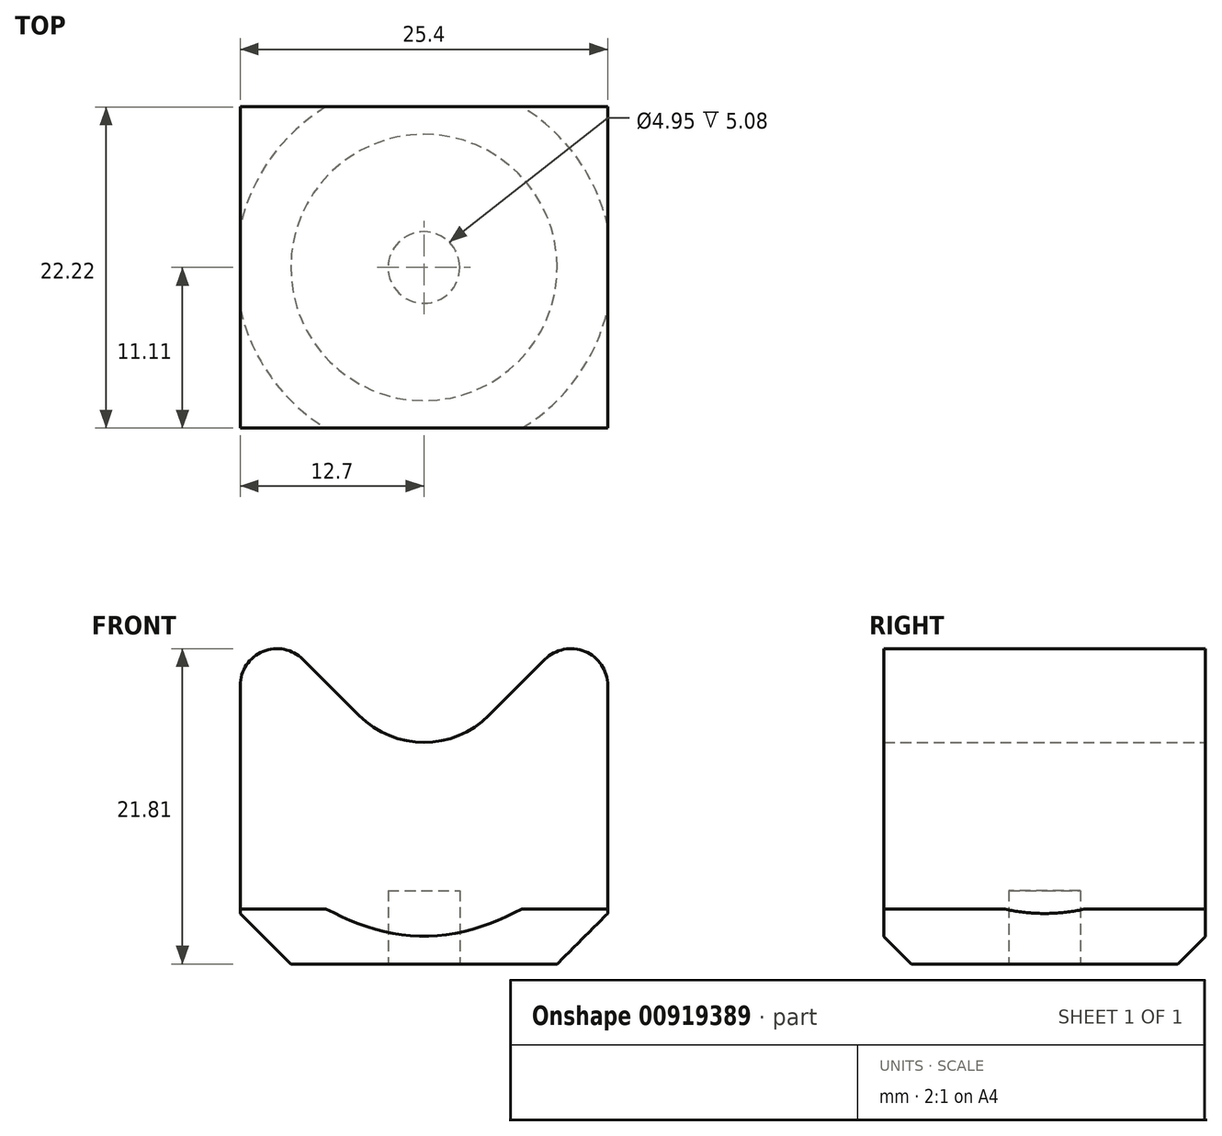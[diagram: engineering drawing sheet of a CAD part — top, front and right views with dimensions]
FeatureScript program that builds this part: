
annotation { "Feature Type Name" : "Feature", "Feature Type Description" : "" }
export const myFeature = defineFeature(function(context is Context, id is Id, definition is map)
    precondition{}
    {
        {
            var Q0;
            Q0=qCreatedBy(makeId("Front.planeOp"),FACE);
            var sketch = newSketch(context, id + "F0", { "sketchPlane" : qUnion([Q0])});
            skLineSegment(sketch, "E0", {"start": v(0, 59) * mm, "end": v(0, -63.05) * mm, "construction": true});
            skLineSegment(sketch, "E1.bottom", {"start": v(-12.7, 12.7) * mm, "end": v(12.7, 12.7) * mm});
            skLineSegment(sketch, "E1.top", {"start": v(-12.7, -12.7) * mm, "end": v(12.7, -12.7) * mm});
            skLineSegment(sketch, "E1.left", {"start": v(-12.7, 12.7) * mm, "end": v(-12.7, -12.7) * mm});
            skLineSegment(sketch, "E1.right", {"start": v(12.7, 12.7) * mm, "end": v(12.7, -12.7) * mm});
            skPoint(sketch, "E1.middle", {"position": v(0, 0) * mm});
            skCircle(sketch, "E2", {"center": v(0, 8.98) * mm, "radius": 6.35 * mm});
            skLineSegment(sketch, "E3", {"start": v(-12.7, 12.7) * mm, "end": v(0, 0) * mm});
            skLineSegment(sketch, "E4", {"start": v(0, 0) * mm, "end": v(12.7, 12.7) * mm});
            skSolve(sketch);
        }
        {
            var Q0;
            Q0=makeQuery(id+"F0.imprint","IMPRINT",FACE,{"disambiguationData":[TD([[makeQuery(id+"F0.imprint","IMPRINT",EDGE,{"derivedFrom":sQuery(id+"F0.wireOp",EDGE,"E1.top")}),1.0]])]});
            var Q1;
            {var subQ0=sQuery(id+"F0.wireOp",EDGE,"E3");var subQ1=sQuery(id+"F0.wireOp",EDGE,"E2");var subQ2=makeQuery(id+"F0.imprint","INTERSECT",VERTEX,{"derivedFrom":[subQ1,subQ0]});Q1=makeQuery(id+"F0.imprint","IMPRINT",FACE,{"disambiguationData":[TD([[makeQuery(id+"F0.imprint","IMPRINT",EDGE,{"disambiguationData":[TD([[subQ2,-1.0]])],"derivedFrom":subQ1}),-1.0]])]});}
            extrude(context, id + "F1", {"entities" : qUnion([Q0, Q1]), "depth" : 22.22 * mm, "offsetDistance" : 25.4 * mm, "symmetric" : true});
        }
        {
            var Q0;
            Q0=makeQuery(id+"F1.opExtrude","SWEPT_EDGE",EDGE,{"disambiguationData":[OSD([sQuery(id+"F0.wireOp",EDGE,"E1.bottom"),sQuery(id+"F0.wireOp",EDGE,"E1.right"),sQuery(id+"F0.wireOp",EDGE,"E4")])]});
            var Q1;
            Q1=makeQuery(id+"F1.opExtrude","SWEPT_EDGE",EDGE,{"disambiguationData":[OSD([sQuery(id+"F0.wireOp",EDGE,"E1.bottom"),sQuery(id+"F0.wireOp",EDGE,"E1.left"),sQuery(id+"F0.wireOp",EDGE,"E3")])]});
            fillet(context, id + "F2", {"entities" : qUnion([Q0, Q1]), "radius" : 2.54 * mm, "tangentPropagation" : true, "allowEdgeOverflow" : false});
        }
        {
            var Q0;
            Q0=makeQuery(id+"F1.opExtrude","SWEPT_FACE",FACE,{"disambiguationData":[OSD([sQuery(id+"F0.wireOp",EDGE,"E1.top")])]});
            var sketch = newSketch(context, id + "F3", { "sketchPlane" : qUnion([Q0])});
            skCircle(sketch, "E5", {"center": v(0, 0) * mm, "radius": 10.95 * mm});
            skCircle(sketch, "E6", {"center": v(0, 0) * mm, "radius": 2.48 * mm});
            skSolve(sketch);
        }
        {
            var Q0;
            Q0=makeQuery(id+"F3.imprint","IMPRINT",FACE,{"disambiguationData":[TD([[makeQuery(id+"F3.imprint","IMPRINT",EDGE,{"derivedFrom":sQuery(id+"F3.wireOp",EDGE,"E6")}),1.0]])]});
            extrude(context, id + "F4", {"entities" : qUnion([Q0]), "operationType" : NewBodyOperationType.REMOVE, "oppositeDirection" : true, "depth" : 5.08 * mm, "offsetDistance" : 25.4 * mm});
        }
        {
            var Q0;
            Q0=makeQuery(id+"F1.opExtrude","SWEPT_FACE",FACE,{"disambiguationData":[OSD([sQuery(id+"F0.wireOp",EDGE,"E1.top")])]});
            var sketch = newSketch(context, id + "F5", { "sketchPlane" : qUnion([Q0])});
            skCircle(sketch, "E7", {"center": v(0, 0) * mm, "radius": 7.94 * mm});
            skSolve(sketch);
        }
        {
            var Q0;
            Q0=makeQuery(id+"F5.imprint","IMPRINT",FACE,{"disambiguationData":[TD([[makeQuery(id+"F5.imprint","IMPRINT",EDGE,{"derivedFrom":sQuery(id+"F5.wireOp",EDGE,"E7")}),-1.0]])]});
            extrude(context, id + "F6", {"entities" : qUnion([Q0]), "operationType" : NewBodyOperationType.REMOVE, "flatOperationType" : FlatOperationType.REMOVE, "oppositeDirection" : true, "depth" : 3.8 * mm, "offsetDistance" : 25.4 * mm, "domain" : OperationDomain.MODEL});
        }
        {
            var Q0;
            Q0=makeQuery(id+"F6.boolean.opBoolean","COPY",EDGE,{"derivedFrom":makeQuery(id+"F6.opExtrude","CAP_EDGE",EDGE,{"disambiguationData":[OSD([sQuery(id+"F5.wireOp",EDGE,"E7")])],"isStart":false})});
            chamfer(context, id + "F7", {"entities" : qUnion([Q0]), "width" : 5.08 * mm, "tangentPropagation" : true});
        }
    });
